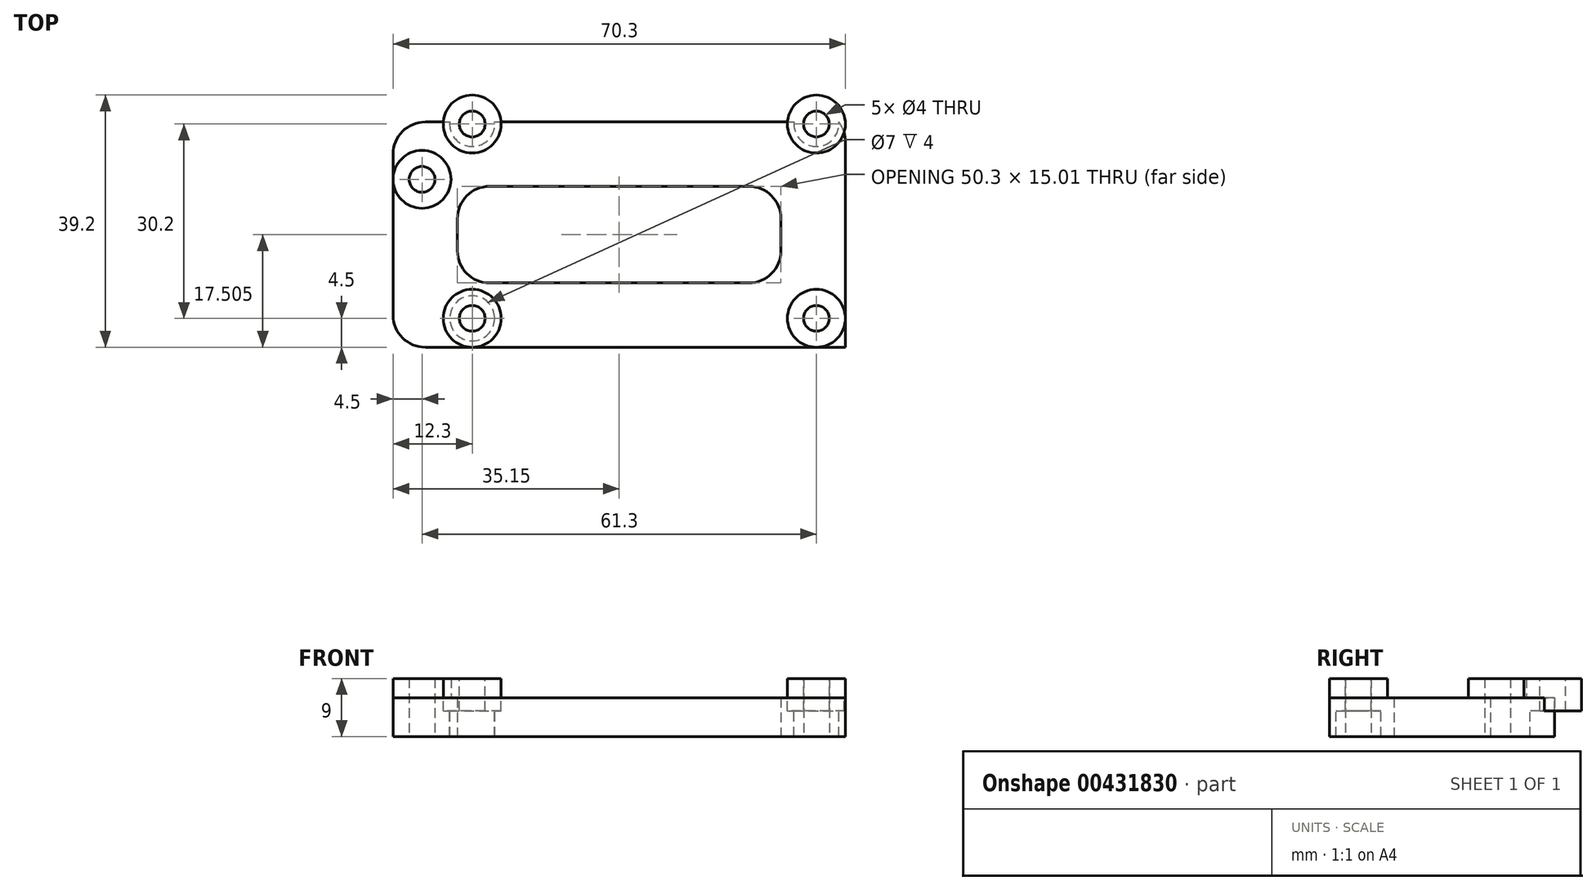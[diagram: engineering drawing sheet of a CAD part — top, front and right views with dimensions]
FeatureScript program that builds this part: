
annotation { "Feature Type Name" : "Feature", "Feature Type Description" : "" }
export const myFeature = defineFeature(function(context is Context, id is Id, definition is map)
    precondition{}
    {
        {
            assignVariable(context, id + "F0", {"name" : "circuitBottomClearing", "anyValue" : 3});
        }
        {
            assignVariable(context, id + "F1", {"name" : "fullHeight", "anyValue" : 9});
        }
        {
            assignVariable(context, id + "F2", {"name" : "baseHeight", "anyValue" : getVariable(context, 'fullHeight') - getVariable(context, 'circuitBottomClearing')});
        }
        {
            assignVariable(context, id + "F3", {"name" : "mountHeight", "anyValue" : 5});
        }
        {
            var Q0;
            Q0=qCreatedBy(makeId("Top.planeOp"),FACE);
            var sketch = newSketch(context, id + "F4", { "sketchPlane" : qUnion([Q0])});
            skLineSegment(sketch, "E0.bottom", {"start": v(-38, 15.5) * mm, "end": v(38.5, 15.5) * mm, "construction": true});
            skLineSegment(sketch, "E0.top", {"start": v(-38, -15.5) * mm, "end": v(38.5, -15.5) * mm, "construction": true});
            skLineSegment(sketch, "E0.left", {"start": v(-38, 15.5) * mm, "end": v(-38, -15.5) * mm, "construction": true});
            skLineSegment(sketch, "E0.right", {"start": v(38.5, 15.5) * mm, "end": v(38.5, -15.5) * mm, "construction": true});
            skLineSegment(sketch, "E1", {"start": v(32.9, 0) * mm, "end": v(32.9, -15.5) * mm, "construction": true});
            skLineSegment(sketch, "E2", {"start": v(38.5, -12.8) * mm, "end": v(-38, -12.8) * mm, "construction": true});
            skLineSegment(sketch, "E3", {"start": v(-38, 12.8) * mm, "end": v(38.5, 12.8) * mm, "construction": true});
            skLineSegment(sketch, "E4", {"start": v(-32.4, 15.5) * mm, "end": v(-32.4, -15.5) * mm, "construction": true});
            skCircle(sketch, "E5", {"center": v(-30.4, 10.8) * mm, "radius": 2 * mm});
            skCircle(sketch, "E6", {"center": v(30.9, -10.8) * mm, "radius": 2 * mm});
            skLineSegment(sketch, "E7", {"start": v(-38, 0) * mm, "end": v(38.5, 0) * mm, "construction": true});
            skCircle(sketch, "E8", {"center": v(-30.4, 10.8) * mm, "radius": 4.5 * mm});
            skCircle(sketch, "E9", {"center": v(30.9, -10.8) * mm, "radius": 4.5 * mm});
            skSolve(sketch);
        }
        {
            var Q0;
            Q0 = qSketchRegion(id + "F4", true);
            extrude(context, id + "F5", {"entities" : qUnion([Q0]), "depth" : (getVariable(context, 'fullHeight')) * mm});
        }
        {
            var Q0;
            Q0=makeQuery(id+"F4.imprint","IMPRINT",FACE,{"disambiguationData":[TD([[makeQuery(id+"F4.imprint","IMPRINT",EDGE,{"derivedFrom":sQuery(id+"F4.wireOp",EDGE,"E5")}),-1.0]])]});
            var sketch = newSketch(context, id + "F6", { "sketchPlane" : qUnion([Q0])});
            skPoint(sketch, "E10.0", {"position": v(-30.4, 10.8) * mm});
            skPoint(sketch, "E11.0", {"position": v(30.9, -10.8) * mm});
            skPoint(sketch, "E12.bottom.start.orphan", {"position": v(31.4, -5.76) * mm});
            skPoint(sketch, "E13.start.orphan", {"position": v(34.07, 18.62) * mm});
            skPoint(sketch, "E12.top.start.orphan", {"position": v(28.62, 18.62) * mm});
            skPoint(sketch, "E14.orphan", {"position": v(-30.4, -11.11) * mm});
            skLineSegment(sketch, "E15.bottom", {"start": v(-24.9, 9.71) * mm, "end": v(25.4, 9.71) * mm});
            skLineSegment(sketch, "E15.top", {"start": v(-24.9, -5.3) * mm, "end": v(25.4, -5.3) * mm});
            skLineSegment(sketch, "E15.left", {"start": v(-24.9, 9.71) * mm, "end": v(-24.9, -5.3) * mm});
            skLineSegment(sketch, "E15.right", {"start": v(25.4, 9.71) * mm, "end": v(25.4, -5.3) * mm});
            skLineSegment(sketch, "E16.bottom", {"start": v(-34.9, 19.71) * mm, "end": v(35.4, 19.71) * mm});
            skLineSegment(sketch, "E16.top", {"start": v(-34.9, -15.3) * mm, "end": v(35.4, -15.3) * mm});
            skLineSegment(sketch, "E16.left", {"start": v(-34.9, 19.71) * mm, "end": v(-34.9, -15.3) * mm});
            skLineSegment(sketch, "E16.right", {"start": v(35.4, 19.71) * mm, "end": v(35.4, -15.3) * mm});
            skSolve(sketch);
        }
        {
            var Q0;
            Q0 = qSketchRegion(id + "F6", true);
            extrude(context, id + "F7", {"entities" : qUnion([Q0]), "operationType" : NewBodyOperationType.ADD, "depth" : (getVariable(context, 'baseHeight')) * mm});
        }
        {
            var Q0;
            Q0=makeQuery(id+"F5.opExtrude","CAP_FACE",FACE,{"disambiguationData":[OSD([sQuery(id+"F4.wireOp",EDGE,"E5"),sQuery(id+"F4.wireOp",EDGE,"E8")])],"isStart":false});
            var sketch = newSketch(context, id + "F8", { "sketchPlane" : qUnion([Q0])});
            skCircle(sketch, "E17", {"center": v(-22.6, -10.8) * mm, "radius": 2 * mm});
            skCircle(sketch, "E18", {"center": v(-22.6, -10.8) * mm, "radius": 4.5 * mm});
            skCircle(sketch, "E19", {"center": v(-22.6, 19.4) * mm, "radius": 2 * mm});
            skCircle(sketch, "E20", {"center": v(-22.6, 19.4) * mm, "radius": 4.5 * mm});
            skCircle(sketch, "E21", {"center": v(30.9, 19.4) * mm, "radius": 2 * mm});
            skCircle(sketch, "E22", {"center": v(30.9, 19.4) * mm, "radius": 4.5 * mm});
            skPoint(sketch, "E23.0", {"position": v(30.9, -10.8) * mm});
            skLineSegment(sketch, "E24.0", {"start": v(38.5, -12.8) * mm, "end": v(-38, -12.8) * mm});
            skLineSegment(sketch, "E25.0", {"start": v(32.9, 0) * mm, "end": v(32.9, -15.5) * mm});
            skLineSegment(sketch, "E26", {"start": v(30.9, -10.8) * mm, "end": v(-38.76, -10.8) * mm, "construction": true});
            skLineSegment(sketch, "E27", {"start": v(-22.6, -10.8) * mm, "end": v(-22.6, 18.3) * mm, "construction": true});
            skLineSegment(sketch, "E28", {"start": v(30.9, -10.8) * mm, "end": v(30.9, 20.43) * mm, "construction": true});
            skLineSegment(sketch, "E29", {"start": v(-22.6, 17.4) * mm, "end": v(30.9, 17.4) * mm, "construction": true});
            skSolve(sketch);
        }
        {
            var Q0;
            Q0 = qSketchRegion(id + "F8", true);
            extrude(context, id + "F9", {"entities" : qUnion([Q0]), "operationType" : NewBodyOperationType.ADD, "oppositeDirection" : true, "depth" : (getVariable(context, 'mountHeight')) * mm});
        }
        {
            var Q0;
            Q0=makeQuery(id+"F9.boolean.opBoolean","MERGE",FACE,{"derivedFrom":[makeQuery(id+"F5.opExtrude","CAP_FACE",FACE,{"disambiguationData":[OSD([sQuery(id+"F4.wireOp",EDGE,"E6"),sQuery(id+"F4.wireOp",EDGE,"E9")])],"isStart":false}),makeQuery(id+"F9.opExtrude","CAP_FACE",FACE,{"disambiguationData":[OSD([sQuery(id+"F8.wireOp",EDGE,"6bb8e593-27b5-4253-ada7-62b1f03044dc.0"),sQuery(id+"F8.wireOp",EDGE,"E24.0"),sQuery(id+"F8.wireOp",EDGE,"E25.0")])],"isStart":true})]});
            var sketch = newSketch(context, id + "F10", { "sketchPlane" : qUnion([Q0])});
            skPoint(sketch, "E30.0", {"position": v(30.9, -10.8) * mm});
            skCircle(sketch, "E31", {"center": v(30.9, -10.8) * mm, "radius": 2 * mm});
            skPoint(sketch, "E32.0", {"position": v(-30.4, 10.8) * mm});
            skCircle(sketch, "E33", {"center": v(-30.4, 10.8) * mm, "radius": 2 * mm});
            skSolve(sketch);
        }
        {
            var Q0;
            Q0 = qSketchRegion(id + "F10", true);
            extrude(context, id + "F11", {"entities" : qUnion([Q0]), "operationType" : NewBodyOperationType.REMOVE, "endBound" : BoundingType.THROUGH_ALL, "oppositeDirection" : true, "depth" : 9 * mm});
        }
        {
            var Q0;
            Q0=makeQuery(id+"F9.opExtrude","CAP_FACE",FACE,{"disambiguationData":[OSD([sQuery(id+"F8.wireOp",EDGE,"E19"),sQuery(id+"F8.wireOp",EDGE,"E20")])],"isStart":true});
            var sketch = newSketch(context, id + "F12", { "sketchPlane" : qUnion([Q0])});
            skCircle(sketch, "E34.0", {"center": v(-22.6, 19.4) * mm, "radius": 2 * mm});
            skCircle(sketch, "E35.0", {"center": v(30.9, 19.4) * mm, "radius": 2 * mm});
            skCircle(sketch, "E36.0", {"center": v(-22.6, -10.8) * mm, "radius": 2 * mm});
            skCircle(sketch, "E37", {"center": v(-22.6, 19.4) * mm, "radius": 3.5 * mm});
            skCircle(sketch, "E38", {"center": v(30.9, 19.4) * mm, "radius": 3.5 * mm});
            skCircle(sketch, "E39", {"center": v(-22.6, -10.8) * mm, "radius": 3.5 * mm});
            skSolve(sketch);
        }
        {
            var Q0;
            Q0 = qSketchRegion(id + "F12", true);
            extrude(context, id + "F13", {"entities" : qUnion([Q0]), "operationType" : NewBodyOperationType.REMOVE, "oppositeDirection" : true, "depth" : 28 * mm, "hasSecondDirection" : true, "secondDirectionOppositeDirection" : true, "secondDirectionDepth" : (getVariable(context, 'mountHeight')) * mm});
        }
        {
            var Q0;
            Q0=makeQuery(id+"F9.opExtrude","CAP_FACE",FACE,{"disambiguationData":[OSD([sQuery(id+"F8.wireOp",EDGE,"E19"),sQuery(id+"F8.wireOp",EDGE,"E20")])],"isStart":true});
            var sketch = newSketch(context, id + "F14", { "sketchPlane" : qUnion([Q0])});
            skCircle(sketch, "E40.0", {"center": v(-22.6, 19.4) * mm, "radius": 2 * mm});
            skCircle(sketch, "E41.0", {"center": v(30.9, 19.4) * mm, "radius": 2 * mm});
            skCircle(sketch, "E42.0", {"center": v(-22.6, -10.8) * mm, "radius": 2 * mm});
            skCircle(sketch, "E43.0", {"center": v(30.9, -10.8) * mm, "radius": 2 * mm});
            skSolve(sketch);
        }
        {
            var Q0;
            Q0 = qSketchRegion(id + "F14", true);
            extrude(context, id + "F15", {"entities" : qUnion([Q0]), "operationType" : NewBodyOperationType.REMOVE, "endBound" : BoundingType.THROUGH_ALL, "oppositeDirection" : true, "depth" : 25 * mm});
        }
        {
            var Q0;
            Q0=makeQuery(id+"F7.opExtrude","SWEPT_EDGE",EDGE,{"disambiguationData":[OSD([sQuery(id+"F6.wireOp",EDGE,"E16.top"),sQuery(id+"F6.wireOp",EDGE,"E16.left")])]});
            var Q1;
            Q1=makeQuery(id+"F7.opExtrude","SWEPT_EDGE",EDGE,{"disambiguationData":[OSD([sQuery(id+"F6.wireOp",EDGE,"E15.top"),sQuery(id+"F6.wireOp",EDGE,"E15.right")])]});
            var Q2;
            Q2=makeQuery(id+"F7.opExtrude","SWEPT_EDGE",EDGE,{"disambiguationData":[OSD([sQuery(id+"F6.wireOp",EDGE,"E15.top"),sQuery(id+"F6.wireOp",EDGE,"E15.left")])]});
            var Q3;
            Q3=makeQuery(id+"F7.opExtrude","SWEPT_EDGE",EDGE,{"disambiguationData":[OSD([sQuery(id+"F6.wireOp",EDGE,"E16.bottom"),sQuery(id+"F6.wireOp",EDGE,"E16.left")])]});
            var Q4;
            Q4=makeQuery(id+"F7.opExtrude","SWEPT_EDGE",EDGE,{"disambiguationData":[OSD([sQuery(id+"F6.wireOp",EDGE,"E15.bottom"),sQuery(id+"F6.wireOp",EDGE,"E15.left")])]});
            var Q5;
            Q5=makeQuery(id+"F7.opExtrude","SWEPT_EDGE",EDGE,{"disambiguationData":[OSD([sQuery(id+"F6.wireOp",EDGE,"E15.bottom"),sQuery(id+"F6.wireOp",EDGE,"E15.right")])]});
            var Q6;
            Q6=makeQuery(id+"F7.opExtrude","SWEPT_EDGE",EDGE,{"disambiguationData":[OSD([sQuery(id+"F6.wireOp",EDGE,"E16.bottom"),sQuery(id+"F6.wireOp",EDGE,"E16.right")])]});
            fillet(context, id + "F16", {"entities" : qUnion([Q0, Q1, Q2, Q3, Q4, Q5, Q6]), "radius" : 5 * mm, "tangentPropagation" : true, "allowEdgeOverflow" : false});
        }
    });
